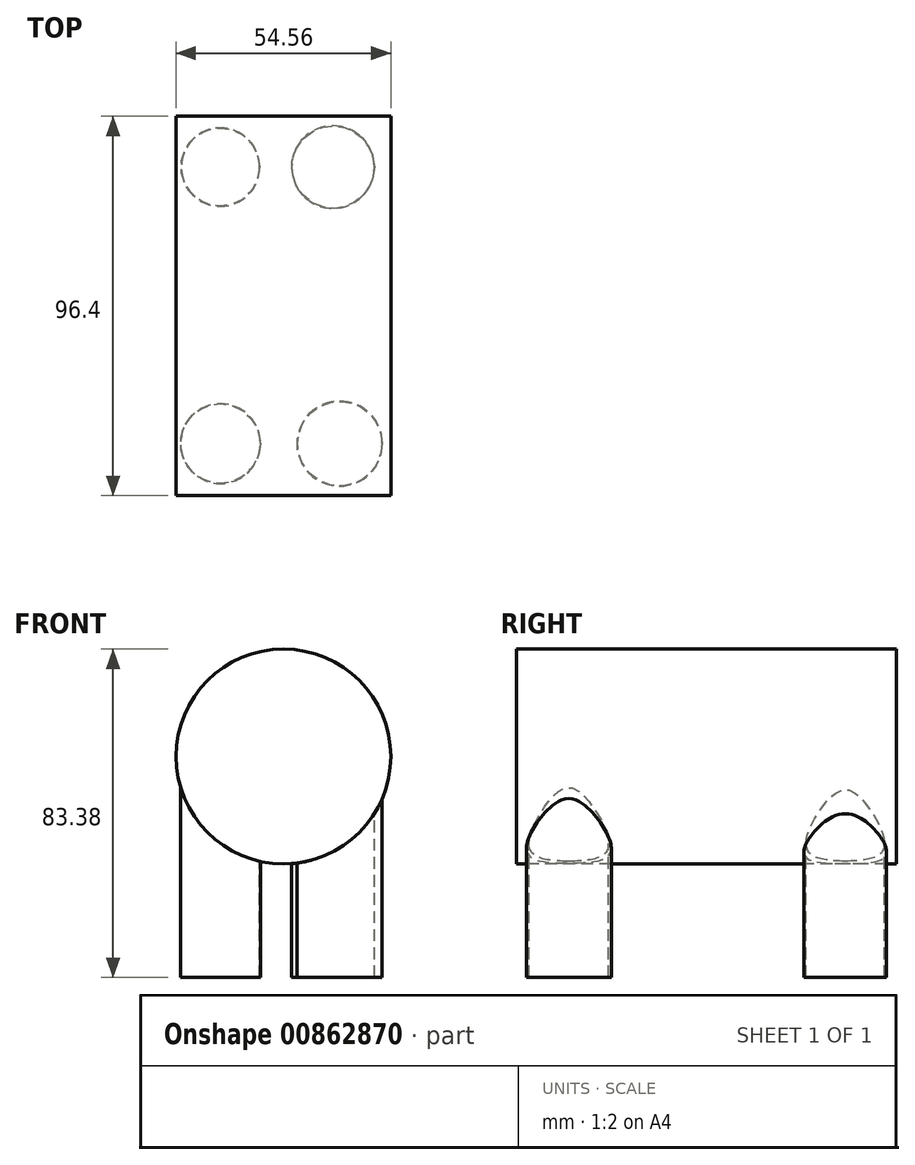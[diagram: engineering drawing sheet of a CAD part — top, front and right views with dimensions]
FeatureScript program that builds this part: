
annotation { "Feature Type Name" : "Feature", "Feature Type Description" : "" }
export const myFeature = defineFeature(function(context is Context, id is Id, definition is map)
    precondition{}
    {
        {
            var Q0;
            Q0=qCreatedBy(makeId("Front.planeOp"),FACE);
            var sketch = newSketch(context, id + "F0", { "sketchPlane" : qUnion([Q0])});
            skCircle(sketch, "E0", {"center": v(0, 0) * mm, "radius": 27.28 * mm});
            skSolve(sketch);
        }
        {
            var Q0;
            Q0 = qSketchRegion(id + "F0", true);
            extrude(context, id + "F1", {"entities" : qUnion([Q0]), "endBound" : BoundingType.SYMMETRIC, "oppositeDirection" : true, "depth" : 96.4 * mm, "offsetDistance" : 25 * mm});
        }
        {
            var Q0;
            Q0=qCreatedBy(makeId("Top.planeOp"),FACE);
            var sketch = newSketch(context, id + "F2", { "sketchPlane" : qUnion([Q0])});
            skCircle(sketch, "E1", {"center": v(-16, -34.98) * mm, "radius": 10.13 * mm});
            skCircle(sketch, "E2", {"center": v(14.3, -34.98) * mm, "radius": 10.79 * mm});
            skCircle(sketch, "E3", {"center": v(-16, 35.27) * mm, "radius": 9.95 * mm});
            skCircle(sketch, "E4", {"center": v(12.6, 35.27) * mm, "radius": 10.48 * mm});
            skSolve(sketch);
        }
        {
            var Q0;
            Q0 = qSketchRegion(id + "F2", true);
            extrude(context, id + "F3", {"entities" : qUnion([Q0]), "operationType" : NewBodyOperationType.ADD, "oppositeDirection" : true, "depth" : 56.1 * mm, "offsetDistance" : 25 * mm});
        }
    });
